# Revit family: Worksurface-Teknion-JNWRSE-Single_Sided_Rectangular_Double_Sided-R2015
name_source: partatom
category: Furniture
revit_build: Autodesk Revit Architecture 2016 (Build: 20150714_1515(x64)
units: mm (PartAtom-declared; Revit-internal decimal feet)

## family parameters
Always vertical = Yes
Cut with Voids When Loaded = No
OmniClass Number = 23.40.20.00
OmniClass Title = General Furniture and Specialties
Room Calculation Point = No
Shared = Yes
Work Plane-Based = No

## types (3) — shared parameters
Assembly Code = E2020200
Description = Single-Sided Rectangular Worksurface – Exposed Beam
Manufacturer = Teknion
Manufacturer Fax = 416.661.4586
Part Number = JNWRSE
Product Documentation Link = http://www.teknion.com
Product Line = Expansion Cityline
Product Page URL = http://www.teknion.com
Series = Expansion Cityline
Sustainability Data = http://www.teknion.com
URL = www.teknion.com
Unit Weight URL = http://www.teknion.com
Warranty = http://www.teknion.com

## per-type parameters (varying)
| type | Depth | Model |
| 24" Depth | 24 " | JNWRSE_24__ |
| 18" Depth | 18 " | JNWRSE_18__ |
| 30" Depth | 30 " | JNWRSE_30__ |

## geometry (parser evidence)
native form markers: Sweep x3
no freeform markers — native parametric forms only
